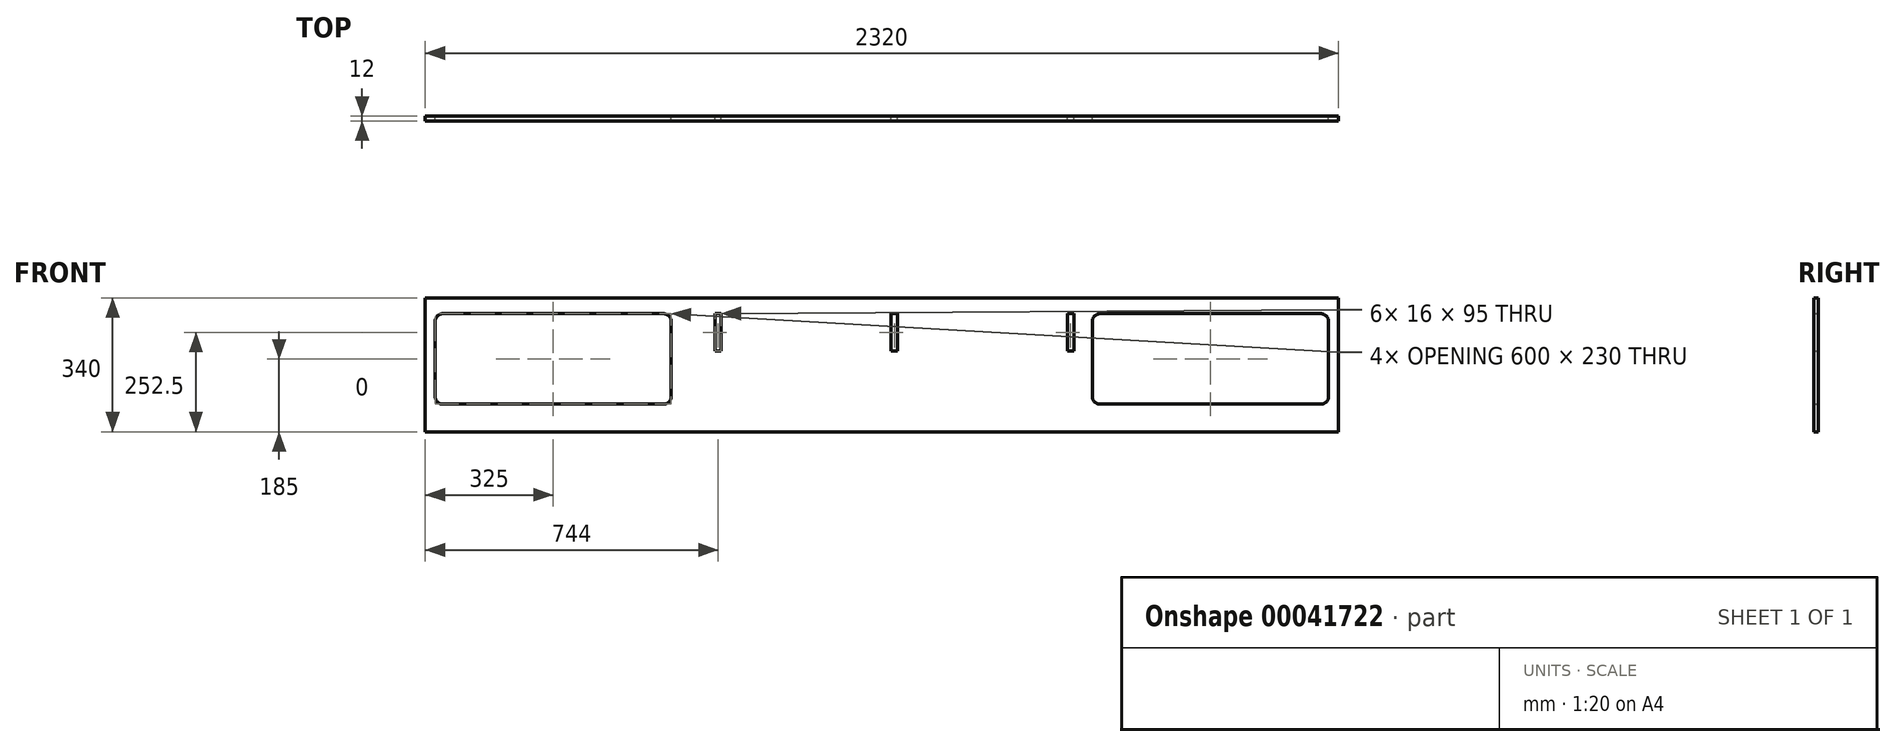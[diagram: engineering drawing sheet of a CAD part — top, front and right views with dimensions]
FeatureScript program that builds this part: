
annotation { "Feature Type Name" : "Feature", "Feature Type Description" : "" }
export const myFeature = defineFeature(function(context is Context, id is Id, definition is map)
    precondition{}
    {
        {
            var Q0;
            Q0=qCreatedBy(makeId("Front.planeOp"),FACE);
            var sketch = newSketch(context, id + "F0", { "sketchPlane" : qUnion([Q0])});
            skLineSegment(sketch, "E0.bottom", {"start": v(0, 0) * mm, "end": v(2320, 0) * mm});
            skLineSegment(sketch, "E0.top", {"start": v(0, 340) * mm, "end": v(2320, 340) * mm});
            skLineSegment(sketch, "E0.left", {"start": v(0, 0) * mm, "end": v(0, 340) * mm});
            skLineSegment(sketch, "E0.right", {"start": v(2320, 0) * mm, "end": v(2320, 340) * mm});
            skLineSegment(sketch, "E1.bottom", {"start": v(45, 300) * mm, "end": v(605, 300) * mm});
            skLineSegment(sketch, "E1.top", {"start": v(45, 70) * mm, "end": v(605, 70) * mm});
            skLineSegment(sketch, "E1.left", {"start": v(25, 280) * mm, "end": v(25, 90) * mm});
            skLineSegment(sketch, "E1.right", {"start": v(625, 280) * mm, "end": v(625, 90) * mm});
            skLineSegment(sketch, "E2.bottom", {"start": v(2275, 300) * mm, "end": v(1715, 300) * mm});
            skLineSegment(sketch, "E2.top", {"start": v(2275, 70) * mm, "end": v(1715, 70) * mm});
            skLineSegment(sketch, "E2.left", {"start": v(2295, 280) * mm, "end": v(2295, 90) * mm});
            skLineSegment(sketch, "E2.right", {"start": v(1695, 280) * mm, "end": v(1695, 90) * mm});
            skLineSegment(sketch, "E3.bottom", {"start": v(1648, 300) * mm, "end": v(1632, 300) * mm});
            skLineSegment(sketch, "E3.top", {"start": v(1648, 205) * mm, "end": v(1632, 205) * mm});
            skLineSegment(sketch, "E3.left", {"start": v(1648, 300) * mm, "end": v(1648, 205) * mm});
            skLineSegment(sketch, "E3.right", {"start": v(1632, 300) * mm, "end": v(1632, 205) * mm});
            skLineSegment(sketch, "E4.bottom", {"start": v(1200, 300) * mm, "end": v(1184, 300) * mm});
            skLineSegment(sketch, "E4.top", {"start": v(1200, 205) * mm, "end": v(1184, 205) * mm});
            skLineSegment(sketch, "E4.left", {"start": v(1200, 300) * mm, "end": v(1200, 205) * mm});
            skLineSegment(sketch, "E4.right", {"start": v(1184, 300) * mm, "end": v(1184, 205) * mm});
            skLineSegment(sketch, "E5.bottom", {"start": v(752, 300) * mm, "end": v(736, 300) * mm});
            skLineSegment(sketch, "E5.top", {"start": v(752, 205) * mm, "end": v(736, 205) * mm});
            skLineSegment(sketch, "E5.left", {"start": v(752, 300) * mm, "end": v(752, 205) * mm});
            skLineSegment(sketch, "E5.right", {"start": v(736, 300) * mm, "end": v(736, 205) * mm});
            skPoint(sketch, "E6.visualSharp", {"position": v(25, 300) * mm});
            skArc(sketch, "E6.filletArc", {"start": v(45, 300) * mm, "mid": v(30.86, 294.14) * mm, "end": v(25, 280) * mm});
            skPoint(sketch, "E7.visualSharp", {"position": v(625, 300) * mm});
            skArc(sketch, "E7.filletArc", {"start": v(625, 280) * mm, "mid": v(619.14, 294.14) * mm, "end": v(605, 300) * mm});
            skPoint(sketch, "E8.visualSharp", {"position": v(625, 70) * mm});
            skArc(sketch, "E8.filletArc", {"start": v(605, 70) * mm, "mid": v(619.14, 75.86) * mm, "end": v(625, 90) * mm});
            skPoint(sketch, "E9.visualSharp", {"position": v(25, 70) * mm});
            skArc(sketch, "E9.filletArc", {"start": v(25, 90) * mm, "mid": v(30.86, 75.86) * mm, "end": v(45, 70) * mm});
            skPoint(sketch, "E10.visualSharp", {"position": v(1695, 300) * mm});
            skArc(sketch, "E10.filletArc", {"start": v(1715, 300) * mm, "mid": v(1700.86, 294.14) * mm, "end": v(1695, 280) * mm});
            skPoint(sketch, "E11.visualSharp", {"position": v(2295, 300) * mm});
            skArc(sketch, "E11.filletArc", {"start": v(2295, 280) * mm, "mid": v(2289.14, 294.14) * mm, "end": v(2275, 300) * mm});
            skPoint(sketch, "E12.visualSharp", {"position": v(2295, 70) * mm});
            skArc(sketch, "E12.filletArc", {"start": v(2275, 70) * mm, "mid": v(2289.14, 75.86) * mm, "end": v(2295, 90) * mm});
            skPoint(sketch, "E13.visualSharp", {"position": v(1695, 70) * mm});
            skArc(sketch, "E13.filletArc", {"start": v(1695, 90) * mm, "mid": v(1700.86, 75.86) * mm, "end": v(1715, 70) * mm});
            skSolve(sketch);
        }
        {
            var Q0;
            Q0=makeQuery(id+"F0.imprint","IMPRINT",FACE,{"disambiguationData":[TD([[makeQuery(id+"F0.imprint","IMPRINT",EDGE,{"derivedFrom":sQuery(id+"F0.wireOp",EDGE,"E0.bottom")}),1.0]])]});
            var sketch = newSketch(context, id + "F1", { "sketchPlane" : qUnion([Q0])});
            skSolve(sketch);
        }
        {
            var Q0;
            Q0=makeQuery(id+"F0.imprint","IMPRINT",FACE,{"disambiguationData":[TD([[makeQuery(id+"F0.imprint","IMPRINT",EDGE,{"derivedFrom":sQuery(id+"F0.wireOp",EDGE,"E0.bottom")}),1.0]])]});
            var Q1;
            Q1=makeQuery(id+"F1.imprint","IMPRINT",FACE,{"disambiguationData":[TD([[makeQuery(id+"F1.imprint","IMPRINT",EDGE,{"derivedFrom":makeQuery(id+"F0.imprint","IMPRINT",EDGE,{"derivedFrom":sQuery(id+"F0.wireOp",EDGE,"E0.bottom")})}),1.0]])]});
            extrude(context, id + "F2", {"entities" : qUnion([Q0, Q1]), "depth" : 12 * mm, "offsetDistance" : 25 * mm});
        }
    });
